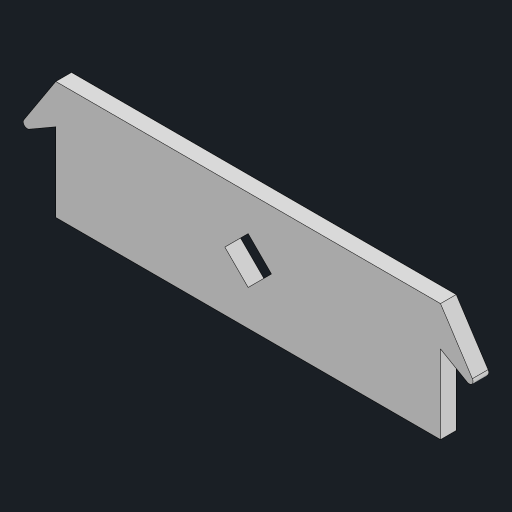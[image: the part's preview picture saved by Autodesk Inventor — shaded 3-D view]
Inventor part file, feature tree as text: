
AUTODESK INVENTOR PART (.ipt)
format: ipt  version: 2023 (Build 270158000, 158)  size: 113,664 bytes
history: native  units: mm
features: other x1, extrude x1, mirror x1, sketch x1
ambient origin geometry x8: Origin, YZ Plane, XZ Plane, XY Plane, X Axis, Y Axis, Z Axis, Center Point
bodies: Body1 (feature_tree)
feature tree (4):
  other  "ソリッド1"
  extrude  "押し出し1"  Depth=4.2mm
  mirror  "ミラー1"
  sketch  "スケッチ1"
